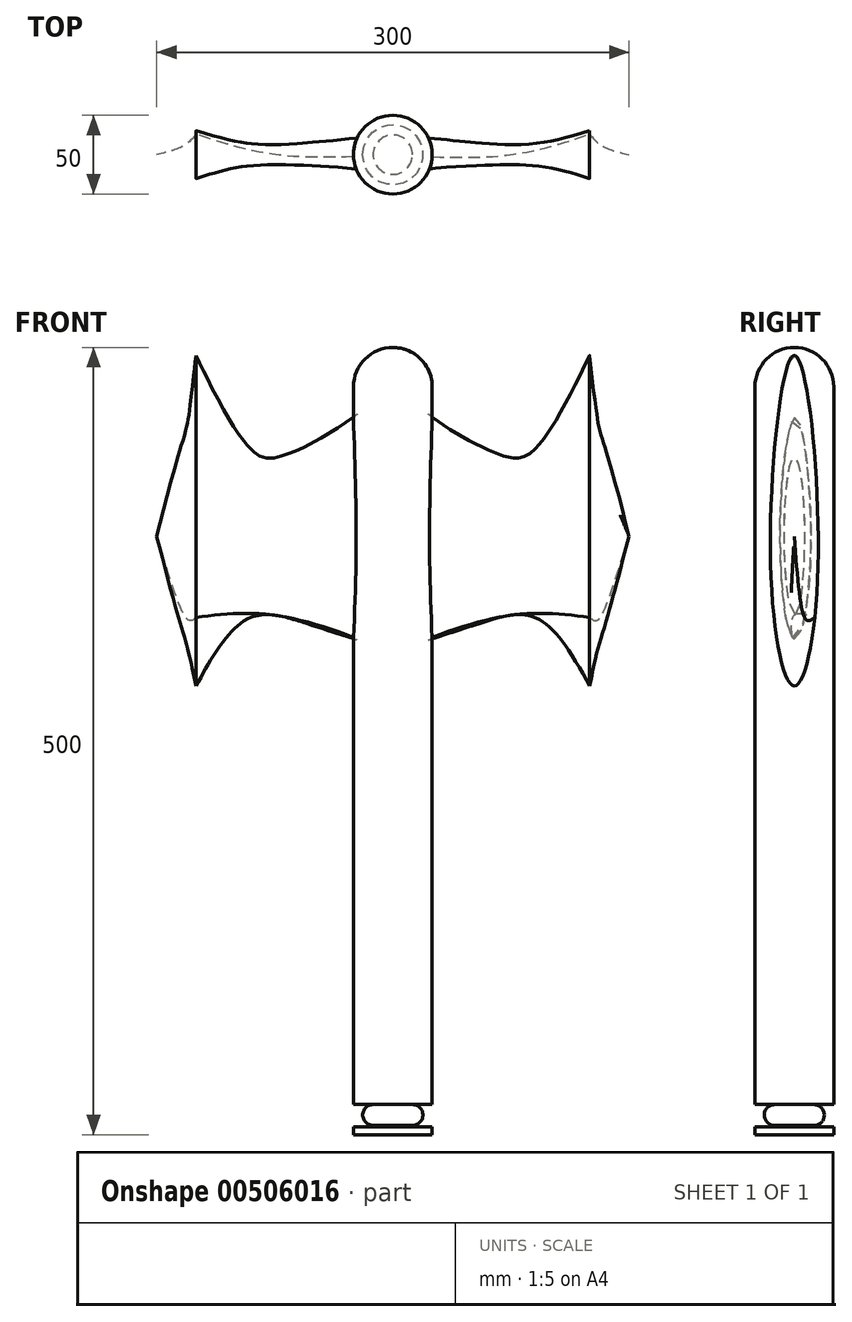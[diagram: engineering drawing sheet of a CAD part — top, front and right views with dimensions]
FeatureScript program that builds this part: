
annotation { "Feature Type Name" : "Feature", "Feature Type Description" : "" }
export const myFeature = defineFeature(function(context is Context, id is Id, definition is map)
    precondition{}
    {
        {
            var Q0;
            Q0=qCreatedBy(makeId("Right.planeOp"),FACE);
            cPlane(context, id + "F0", {"entities" : qUnion([Q0]), "cplaneType" : CPlaneType.OFFSET, "offset" : 12.5 * mm, "width" : 150 * mm, "height" : 150 * mm});
        }
        {
            var Q0;
            Q0=qCreatedBy(id+"F0.planeOp",FACE);
            cPlane(context, id + "F1", {"entities" : qUnion([Q0]), "cplaneType" : CPlaneType.OFFSET, "offset" : 75 * mm, "width" : 150 * mm, "height" : 150 * mm});
        }
        {
            var Q0;
            Q0=qCreatedBy(id+"F1.planeOp",FACE);
            cPlane(context, id + "F2", {"entities" : qUnion([Q0]), "cplaneType" : CPlaneType.OFFSET, "offset" : 50 * mm, "width" : 150 * mm, "height" : 150 * mm});
        }
        {
            var Q0;
            Q0=qCreatedBy(id+"F2.planeOp",FACE);
            cPlane(context, id + "F3", {"entities" : qUnion([Q0]), "cplaneType" : CPlaneType.OFFSET, "offset" : 25 * mm, "width" : 150 * mm, "height" : 150 * mm});
        }
        {
            var Q0;
            Q0=qCreatedBy(id+"F3.planeOp",FACE);
            cPlane(context, id + "F4", {"entities" : qUnion([Q0]), "cplaneType" : CPlaneType.OFFSET, "offset" : 17.5 * mm, "oppositeDirection" : true, "width" : 150 * mm, "height" : 150 * mm});
        }
        {
            var Q0;
            Q0=qCreatedBy(makeId("Front.planeOp"),FACE);
            var sketch = newSketch(context, id + "F5", { "sketchPlane" : qUnion([Q0])});
            skLineSegment(sketch, "E0.bottom", {"start": v(12.5, -225) * mm, "end": v(-12.5, -225) * mm});
            skLineSegment(sketch, "E0.top", {"start": v(12.5, 225) * mm, "end": v(-12.5, 225) * mm});
            skLineSegment(sketch, "E0.left", {"start": v(12.5, -225) * mm, "end": v(12.5, 225) * mm});
            skLineSegment(sketch, "E0.right", {"start": v(-12.5, -225) * mm, "end": v(-12.5, 225) * mm});
            skPoint(sketch, "E0.middle", {"position": v(0, 0) * mm});
            skLineSegment(sketch, "E1.bottom", {"start": v(12.5, -225) * mm, "end": v(0, -225) * mm});
            skLineSegment(sketch, "E1.top", {"start": v(12.5, -250) * mm, "end": v(0, -250) * mm});
            skLineSegment(sketch, "E1.left", {"start": v(12.5, -225) * mm, "end": v(12.5, -250) * mm});
            skLineSegment(sketch, "E1.right", {"start": v(0, -225) * mm, "end": v(0, -250) * mm});
            skLineSegment(sketch, "E2.bottom", {"start": v(0, -250) * mm, "end": v(-12.5, -250) * mm});
            skLineSegment(sketch, "E2.top", {"start": v(0, -245) * mm, "end": v(-12.5, -245) * mm});
            skLineSegment(sketch, "E2.left", {"start": v(0, -245) * mm, "end": v(0, -250) * mm});
            skLineSegment(sketch, "E2.right", {"start": v(-12.5, -245) * mm, "end": v(-12.5, -250) * mm});
            skCircle(sketch, "E3", {"center": v(0, -237.5) * mm, "radius": 6.63 * mm});
            skLineSegment(sketch, "E4.bottom", {"start": v(-12.5, -225) * mm, "end": v(0, -225) * mm});
            skLineSegment(sketch, "E4.top", {"start": v(-12.5, -230.87) * mm, "end": v(0, -230.87) * mm});
            skLineSegment(sketch, "E4.left", {"start": v(-12.5, -225) * mm, "end": v(-12.5, -230.87) * mm});
            skLineSegment(sketch, "E4.right", {"start": v(0, -225) * mm, "end": v(0, -230.87) * mm});
            skArc(sketch, "E5", {"start": v(12.5, 250) * mm, "mid": v(-5.18, 242.68) * mm, "end": v(-12.5, 225) * mm});
            skLineSegment(sketch, "E6", {"start": v(12.5, 225) * mm, "end": v(12.5, 315.15) * mm});
            skSolve(sketch);
        }
        {
            var Q0;
            Q0=qCreatedBy(id+"F0.planeOp",FACE);
            var sketch = newSketch(context, id + "F6", { "sketchPlane" : qUnion([Q0])});
            skLineSegment(sketch, "E7.bottom", {"start": v(12.5, -225) * mm, "end": v(-12.5, -225) * mm, "construction": true});
            skLineSegment(sketch, "E7.top", {"start": v(12.5, 225) * mm, "end": v(-12.5, 225) * mm, "construction": true});
            skLineSegment(sketch, "E7.left", {"start": v(12.5, -225) * mm, "end": v(12.5, 225) * mm, "construction": true});
            skLineSegment(sketch, "E7.right", {"start": v(-12.5, -225) * mm, "end": v(-12.5, 225) * mm, "construction": true});
            skPoint(sketch, "E7.middle", {"position": v(0, 0) * mm});
            skLineSegment(sketch, "E8", {"start": v(0, 0) * mm, "end": v(0, 112.5) * mm, "construction": true});
            skPoint(sketch, "E8.endSnap0", {"position": v(0, 225) * mm});
            skLineSegment(sketch, "E9", {"start": v(0, 0) * mm, "end": v(0, 56.25) * mm, "construction": true});
            skPoint(sketch, "E10", {"position": v(0, 56.25) * mm});
            skPoint(sketch, "E11", {"position": v(12.5, 112.5) * mm});
            skEllipticalArc(sketch, "E12", {});
            skFitSpline(sketch, "E13", {"points": [v(0, 56.25) * mm, v(12.5, 112.5) * mm, v(0, 225) * mm, v(-12.5, 112.5) * mm, v(0, 56.25) * mm]});
            const initialGuessF6  = {"E12": [0, 0.1125, 1, 0, 0.0125, 0.05625, 3.141592653589793, 6.283185307179586]};
            skSetInitialGuess(sketch, initialGuessF6);
            skSolve(sketch);
        }
        {
            var Q0;
            Q0=qCreatedBy(id+"F1.planeOp",FACE);
            var sketch = newSketch(context, id + "F7", { "sketchPlane" : qUnion([Q0])});
            skPoint(sketch, "E14", {"position": v(-75, 130) * mm});
            skPoint(sketch, "E15", {"position": v(75, 130) * mm});
            skPoint(sketch, "E16", {"position": v(0, 130) * mm});
            skLineSegment(sketch, "E17", {"start": v(-75, 130) * mm, "end": v(0, 130) * mm, "construction": true});
            skLineSegment(sketch, "E18", {"start": v(0, 130) * mm, "end": v(75, 130) * mm, "construction": true});
            skLineSegment(sketch, "E19", {"start": v(0, 0) * mm, "end": v(0, 130) * mm, "construction": true});
            skLineSegment(sketch, "E20", {"start": v(0, 130) * mm, "end": v(0, 180) * mm, "construction": true});
            skEllipse(sketch, "E21", {"center": v(0, 130) * mm, "majorRadius": 50 * mm, "minorRadius": 6.41 * mm, "majorAxis": v(0, 1)});
            skSolve(sketch);
        }
        {
            var Q0;
            Q0=qCreatedBy(id+"F2.planeOp",FACE);
            var sketch = newSketch(context, id + "F8", { "sketchPlane" : qUnion([Q0])});
            skLineSegment(sketch, "E22", {"start": v(0, 0) * mm, "end": v(0, 35) * mm, "construction": true});
            skLineSegment(sketch, "E23", {"start": v(0, 35) * mm, "end": v(0, 245) * mm, "construction": true});
            skLineSegment(sketch, "E24", {"start": v(0, 35) * mm, "end": v(-15, 35) * mm, "construction": true});
            skLineSegment(sketch, "E25", {"start": v(-15, 35) * mm, "end": v(-15, 110) * mm, "construction": true});
            skLineSegment(sketch, "E26", {"start": v(0, 110) * mm, "end": v(15, 110) * mm, "construction": true});
            skFitSpline(sketch, "E27", {"points": [v(0, 35) * mm, v(-15, 110) * mm, v(0, 245) * mm, v(15, 110) * mm, v(0, 35) * mm]});
            skSolve(sketch);
        }
        {
            var Q0;
            Q0=qCreatedBy(id+"F3.planeOp",FACE);
            var sketch = newSketch(context, id + "F9", { "sketchPlane" : qUnion([Q0])});
            skLineSegment(sketch, "E28", {"start": v(0, 0) * mm, "end": v(0, 130) * mm, "construction": true});
            skSolve(sketch);
        }
        {
            var Q0;
            Q0=qCreatedBy(id+"F4.planeOp",FACE);
            var sketch = newSketch(context, id + "F10", { "sketchPlane" : qUnion([Q0])});
            skLineSegment(sketch, "E29", {"start": v(0, 0) * mm, "end": v(0, 130) * mm, "construction": true});
            skEllipse(sketch, "E30", {"center": v(0, 130) * mm, "majorRadius": 63.75 * mm, "minorRadius": 9.44 * mm, "majorAxis": v(0, -1)});
            skLineSegment(sketch, "E31", {"start": v(0, 130) * mm, "end": v(0, 66.25) * mm, "construction": true});
            skSolve(sketch);
        }
        {
            var Q0;
            Q0 = qSketchRegion(id + "F5", true);
            var Q1;
            Q1=sQuery(id+"F5.wireOp",EDGE,"E0.left");
            revolve(context, id + "F11", {"entities" : qUnion([Q0]), "axis" : qUnion([Q1]), "revolveType" : RevolveType.FULL});
        }
        {
            var Q0;
            {var subQ0=sQuery(id+"F6.wireOp",EDGE,"E13");var subQ1=sQuery(id+"F6.wireOp",EDGE,"E12");var subQ2=makeQuery(id+"F6.imprint","INTERSECT",VERTEX,{"disambiguationData":[OD(1.0)],"derivedFrom":[subQ1,subQ0]});Q0=makeQuery(id+"F6.imprint","IMPRINT",FACE,{"disambiguationData":[TD([[makeQuery(id+"F6.imprint","IMPRINT",EDGE,{"disambiguationData":[TD([[subQ2,1.0]])],"derivedFrom":subQ0}),1.0]])]});}
            var Q1;
            Q1=makeQuery(id+"F7.imprint","IMPRINT",FACE,{"disambiguationData":[TD([[makeQuery(id+"F7.imprint","IMPRINT",EDGE,{"derivedFrom":sQuery(id+"F7.wireOp",EDGE,"E21")}),1.0]])]});
            var Q2;
            Q2=makeQuery(id+"F8.imprint","IMPRINT",FACE,{"disambiguationData":[TD([[makeQuery(id+"F8.imprint","IMPRINT",EDGE,{"derivedFrom":sQuery(id+"F8.wireOp",EDGE,"E27")}),-1.0]])]});
            loft(context, id + "F12", {"sheetProfilesArray" : [{ "sheetProfileEntities" : qUnion([Q0]) }, { "sheetProfileEntities" : qUnion([Q1]) }, { "sheetProfileEntities" : qUnion([Q2]) }]});
        }
        {
            var Q1;
            Q1=makeQuery(id+"F12.opLoft","CAP_FACE",FACE,{"disambiguationData":[OSD([makeQuery(id+"F8.imprint","IMPRINT",FACE,{"disambiguationData":[TD([[makeQuery(id+"F8.imprint","IMPRINT",EDGE,{"derivedFrom":sQuery(id+"F8.wireOp",EDGE,"E27")}),-1.0]])]})])],"isStart":true});
            var Q2;
            Q2=makeQuery(id+"F10.imprint","IMPRINT",FACE,{"disambiguationData":[TD([[makeQuery(id+"F10.imprint","IMPRINT",EDGE,{"derivedFrom":sQuery(id+"F10.wireOp",EDGE,"E30")}),1.0]])]});
            var Q3;
            Q3=sQuery(id+"F9.wireOp",VERTEX,"E28.end");
            loft(context, id + "F13", {"operationType" : NewBodyOperationType.ADD, "sheetProfilesArray" : [{ "sheetProfileEntities" : qUnion([Q1]) }, { "sheetProfileEntities" : qUnion([Q2]) }, { "sheetProfileEntities" : qUnion([Q3]) }]});
        }
        {
            var Q0;
            {var subQ0=sQuery(id+"F6.wireOp",EDGE,"E13");var subQ1=sQuery(id+"F6.wireOp",EDGE,"E12");var subQ2=makeQuery(id+"F6.imprint","INTERSECT",VERTEX,{"disambiguationData":[OD(1.0)],"derivedFrom":[subQ1,subQ0]});Q0=makeQuery(id+"F12.opLoft","SWEPT_BODY",BODY,{"disambiguationData":[OSD([makeQuery(id+"F6.imprint","IMPRINT",FACE,{"disambiguationData":[TD([[makeQuery(id+"F6.imprint","IMPRINT",EDGE,{"disambiguationData":[TD([[subQ2,1.0]])],"derivedFrom":subQ0}),1.0]])]}),sQuery(id+"F7.wireOp",EDGE,"E21"),makeQuery(id+"F8.imprint","IMPRINT",FACE,{"disambiguationData":[TD([[makeQuery(id+"F8.imprint","IMPRINT",EDGE,{"derivedFrom":sQuery(id+"F8.wireOp",EDGE,"E27")}),-1.0]])]})])]});}
            var Q1;
            Q1=qCreatedBy(id+"F0.planeOp",FACE);
            mirror(context, id + "F14", {"operationType" : NewBodyOperationType.ADD, "entities" : qUnion([Q0]), "mirrorPlane" : qUnion([Q1])});
        }
    });
